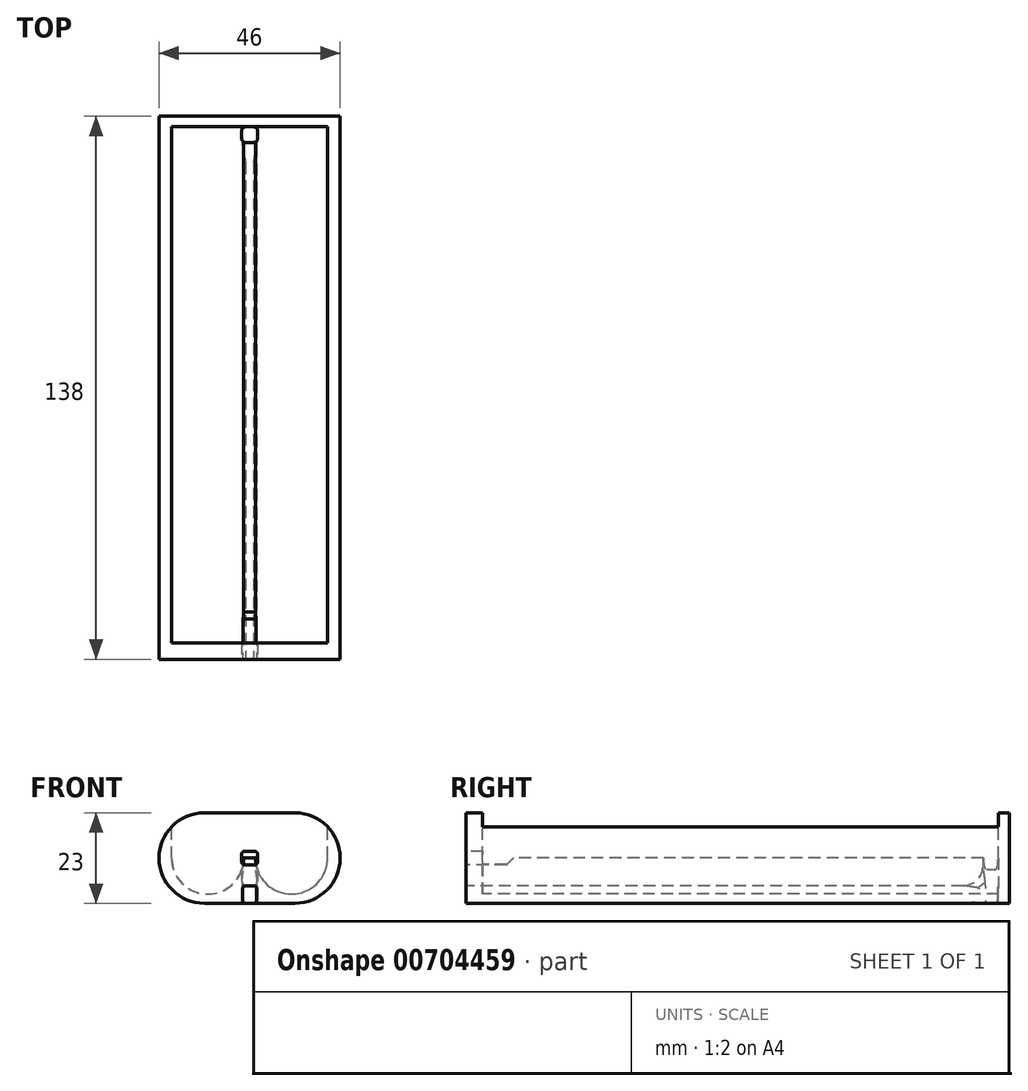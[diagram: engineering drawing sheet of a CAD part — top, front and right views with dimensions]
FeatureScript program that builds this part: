
annotation { "Feature Type Name" : "Feature", "Feature Type Description" : "" }
export const myFeature = defineFeature(function(context is Context, id is Id, definition is map)
    precondition{}
    {
        {
            var Q0;
            Q0=qCreatedBy(makeId("Front.planeOp"),FACE);
            var sketch = newSketch(context, id + "F0", { "sketchPlane" : qUnion([Q0])});
            skCircle(sketch, "E0", {"center": v(-11.5, 0) * mm, "radius": 11.5 * mm});
            skCircle(sketch, "E1", {"center": v(11.5, 0) * mm, "radius": 11.5 * mm});
            skLineSegment(sketch, "E2", {"start": v(-11.5, 11.5) * mm, "end": v(11.5, 11.5) * mm});
            skLineSegment(sketch, "E3", {"start": v(-11.5, -11.5) * mm, "end": v(11.5, -11.5) * mm});
            skSolve(sketch);
        }
        {
            var Q0;
            {var subQ0=sQuery(id+"F0.wireOp",EDGE,"E1");var subQ1=makeQuery(id+"F0.imprint","INTERSECT",VERTEX,{"derivedFrom":[subQ0,sQuery(id+"F0.wireOp",EDGE,"E2")]});Q0=makeQuery(id+"F0.imprint","IMPRINT",FACE,{"disambiguationData":[TD([[makeQuery(id+"F0.imprint","IMPRINT",EDGE,{"disambiguationData":[TD([[subQ1,1.0]])],"derivedFrom":subQ0}),1.0]])]});}
            var Q1;
            {var subQ0=sQuery(id+"F0.wireOp",EDGE,"E0");var subQ1=makeQuery(id+"F0.imprint","INTERSECT",VERTEX,{"derivedFrom":[subQ0,sQuery(id+"F0.wireOp",EDGE,"E3")]});Q1=makeQuery(id+"F0.imprint","IMPRINT",FACE,{"disambiguationData":[TD([[makeQuery(id+"F0.imprint","IMPRINT",EDGE,{"disambiguationData":[TD([[subQ1,-1.0]])],"derivedFrom":subQ0}),1.0]])]});}
            var Q2;
            {var subQ0=sQuery(id+"F0.wireOp",EDGE,"E2");Q2=makeQuery(id+"F0.imprint","IMPRINT",FACE,{"disambiguationData":[TD([[makeQuery(id+"F0.imprint","IMPRINT",EDGE,{"derivedFrom":subQ0}),-1.0]])]});}
            var Q3;
            {var subQ0=sQuery(id+"F0.wireOp",EDGE,"E3");Q3=makeQuery(id+"F0.imprint","IMPRINT",FACE,{"disambiguationData":[TD([[makeQuery(id+"F0.imprint","IMPRINT",EDGE,{"derivedFrom":subQ0}),1.0]])]});}
            extrude(context, id + "F1", {"entities" : qUnion([Q0, Q1, Q2, Q3]), "oppositeDirection" : true, "depth" : 138 * mm, "offsetDistance" : 25 * mm});
        }
        {
            var Q0;
            Q0=makeQuery(id+"F1.opExtrude","SWEPT_FACE",FACE,{"disambiguationData":[OSD([sQuery(id+"F0.wireOp",EDGE,"E2")])]});
            var sketch = newSketch(context, id + "F2", { "sketchPlane" : qUnion([Q0])});
            skLineSegment(sketch, "E4", {"start": v(0, 0) * mm, "end": v(0, 138) * mm, "construction": true});
            skLineSegment(sketch, "E5", {"start": v(0, 130.4) * mm, "end": v(18.2, 130.4) * mm, "construction": true});
            skLineSegment(sketch, "E6", {"start": v(0, 65.2) * mm, "end": v(18.2, 65.2) * mm, "construction": true});
            skLineSegment(sketch, "E7", {"start": v(0, 0) * mm, "end": v(18.2, 0) * mm, "construction": true});
            skSolve(sketch);
        }
        {
            var Q0;
            {var subQ0=sQuery(id+"F0.wireOp",EDGE,"E2");Q0=makeQuery(id+"F2.imprint","IMPRINT",FACE,{"disambiguationData":[TD([[makeQuery(id+"F2.imprint","IMPRINT",EDGE,{"derivedFrom":makeQuery(id+"F1.opExtrude","CAP_EDGE",EDGE,{"disambiguationData":[OSD([subQ0])],"isStart":true})}),1.0]])]});}
            var sketch = newSketch(context, id + "F3", { "sketchPlane" : qUnion([Q0])});
            skLineSegment(sketch, "E8.bottom", {"start": v(2.42, 69.2) * mm, "end": v(20.72, 69.2) * mm, "construction": true});
            skLineSegment(sketch, "E8.top", {"start": v(2.42, 4.2) * mm, "end": v(20.72, 4.2) * mm, "construction": true});
            skLineSegment(sketch, "E8.left", {"start": v(2.42, 69.2) * mm, "end": v(2.42, 4.2) * mm, "construction": true});
            skLineSegment(sketch, "E8.right", {"start": v(20.72, 69.2) * mm, "end": v(20.72, 4.2) * mm, "construction": true});
            skLineSegment(sketch, "E9.0.1.0", {"start": v(2.42, 135.3) * mm, "end": v(20.72, 135.3) * mm, "construction": true});
            skLineSegment(sketch, "E9.0.1.1", {"start": v(20.72, 135.3) * mm, "end": v(20.72, 70.3) * mm, "construction": true});
            skLineSegment(sketch, "E9.0.1.2", {"start": v(2.42, 135.3) * mm, "end": v(2.42, 70.3) * mm, "construction": true});
            skLineSegment(sketch, "E9.0.1.3", {"start": v(2.42, 70.3) * mm, "end": v(20.72, 70.3) * mm, "construction": true});
            skLineSegment(sketch, "E9.1.0.0", {"start": v(-20.68, 69.2) * mm, "end": v(-2.38, 69.2) * mm, "construction": true});
            skLineSegment(sketch, "E9.1.0.1", {"start": v(-2.38, 69.2) * mm, "end": v(-2.38, 4.2) * mm, "construction": true});
            skLineSegment(sketch, "E9.1.0.2", {"start": v(-20.68, 69.2) * mm, "end": v(-20.68, 4.2) * mm, "construction": true});
            skLineSegment(sketch, "E9.1.0.3", {"start": v(-20.68, 4.2) * mm, "end": v(-2.38, 4.2) * mm, "construction": true});
            skLineSegment(sketch, "E9.1.1.0", {"start": v(-20.68, 135.3) * mm, "end": v(-2.38, 135.3) * mm, "construction": true});
            skLineSegment(sketch, "E9.1.1.1", {"start": v(-2.38, 135.3) * mm, "end": v(-2.38, 70.3) * mm, "construction": true});
            skLineSegment(sketch, "E9.1.1.2", {"start": v(-20.68, 135.3) * mm, "end": v(-20.68, 70.3) * mm, "construction": true});
            skLineSegment(sketch, "E9.1.1.3", {"start": v(-20.68, 70.3) * mm, "end": v(-2.38, 70.3) * mm, "construction": true});
            skLineSegment(sketch, "E9.direction1", {"start": v(2.42, 4.2) * mm, "end": v(-20.68, 4.2) * mm, "construction": true});
            skLineSegment(sketch, "E9.direction2", {"start": v(2.42, 4.2) * mm, "end": v(2.42, 70.3) * mm, "construction": true});
            skSolve(sketch);
        }
        {
            var Q0;
            Q0=sQuery(id+"F3.wireOp",EDGE,"E8.top");
            var Q1;
            Q1=makeQuery(id+"F1.opExtrude","CAP_FACE",FACE,{"disambiguationData":[OSD([sQuery(id+"F0.wireOp",EDGE,"E0"),sQuery(id+"F0.wireOp",EDGE,"E1"),sQuery(id+"F0.wireOp",EDGE,"E2"),sQuery(id+"F0.wireOp",EDGE,"E3")])],"isStart":true});
            cPlane(context, id + "F4", {"entities" : qUnion([Q0, Q1]), "cplaneType" : CPlaneType.LINE_ANGLE, "offset" : 25 * mm, "angle" : 0 * degree, "width" : 150 * mm, "height" : 150 * mm});
        }
        {
            var Q0;
            Q0=qCreatedBy(id+"F4.planeOp",FACE);
            var sketch = newSketch(context, id + "F5", { "sketchPlane" : qUnion([Q0])});
            skCircle(sketch, "E10", {"center": v(-10.65, 0) * mm, "radius": 9.15 * mm});
            skCircle(sketch, "E11.MirrorC", {"center": v(10.65, 0) * mm, "radius": 9.15 * mm});
            skLineSegment(sketch, "E12", {"start": v(-19.8, 0) * mm, "end": v(-19.8, 11.5) * mm});
            skLineSegment(sketch, "E13", {"start": v(-19.8, 11.5) * mm, "end": v(19.8, 11.5) * mm});
            skLineSegment(sketch, "E14", {"start": v(19.8, 0) * mm, "end": v(19.8, 11.5) * mm});
            skLineSegment(sketch, "E15", {"start": v(1.5, 0) * mm, "end": v(-1.5, 0) * mm});
            skSolve(sketch);
        }
        {
            var Q0;
            Q0 = qSketchRegion(id + "F5", true);
            var Q1;
            Q1=sQuery(id+"F3.wireOp",VERTEX,"E9.0.1.0.start");
            extrude(context, id + "F6", {"entities" : qUnion([Q0]), "operationType" : NewBodyOperationType.REMOVE, "endBound" : BoundingType.UP_TO_VERTEX, "depth" : 25 * mm, "endBoundEntityVertex" : qUnion([Q1]), "offsetDistance" : 25 * mm});
        }
        {
            var Q0;
            Q0=makeQuery(id+"F1.opExtrude","CAP_FACE",FACE,{"disambiguationData":[OSD([sQuery(id+"F0.wireOp",EDGE,"E0"),sQuery(id+"F0.wireOp",EDGE,"E1"),sQuery(id+"F0.wireOp",EDGE,"E2"),sQuery(id+"F0.wireOp",EDGE,"E3")])],"isStart":true});
            var sketch = newSketch(context, id + "F7", { "sketchPlane" : qUnion([Q0])});
            skLineSegment(sketch, "E16.bottom", {"start": v(1, -11.5) * mm, "end": v(-1, -11.5) * mm});
            skLineSegment(sketch, "E16.top", {"start": v(1, -7) * mm, "end": v(-1, -7) * mm});
            skLineSegment(sketch, "E16.left", {"start": v(1.75, -10.75) * mm, "end": v(1.75, -7.75) * mm});
            skLineSegment(sketch, "E16.right", {"start": v(-1.75, -10.75) * mm, "end": v(-1.75, -7.75) * mm});
            skPoint(sketch, "E16.middle", {"position": v(0, -9.25) * mm});
            skPoint(sketch, "E17.visualSharp", {"position": v(1.75, -7) * mm});
            skArc(sketch, "E17.filletArc", {"start": v(1.75, -7.75) * mm, "mid": v(1.53, -7.22) * mm, "end": v(1, -7) * mm});
            skPoint(sketch, "E18.visualSharp", {"position": v(-1.75, -7) * mm});
            skArc(sketch, "E18.filletArc", {"start": v(-1, -7) * mm, "mid": v(-1.53, -7.22) * mm, "end": v(-1.75, -7.75) * mm});
            skPoint(sketch, "E19.visualSharp", {"position": v(-1.75, -11.5) * mm});
            skArc(sketch, "E19.filletArc", {"start": v(-1.75, -10.75) * mm, "mid": v(-1.53, -11.28) * mm, "end": v(-1, -11.5) * mm});
            skPoint(sketch, "E20.visualSharp", {"position": v(1.75, -11.5) * mm});
            skArc(sketch, "E20.filletArc", {"start": v(1, -11.5) * mm, "mid": v(1.53, -11.28) * mm, "end": v(1.75, -10.75) * mm});
            skSolve(sketch);
        }
        {
            var Q0;
            Q0=makeQuery(id+"F7.imprint","IMPRINT",FACE,{"disambiguationData":[TD([[makeQuery(id+"F7.imprint","IMPRINT",EDGE,{"derivedFrom":sQuery(id+"F7.wireOp",EDGE,"E16.bottom")}),1.0]])]});
            var Q1;
            Q1=makeQuery(id+"F6.boolean.opBoolean","COPY",FACE,{"derivedFrom":makeQuery(id+"F6.opExtrude","CAP_FACE",FACE,{"disambiguationData":[OSD([sQuery(id+"F5.wireOp",EDGE,"E10"),sQuery(id+"F5.wireOp",EDGE,"E11.MirrorC"),sQuery(id+"F5.wireOp",EDGE,"E12"),sQuery(id+"F5.wireOp",EDGE,"E13"),sQuery(id+"F5.wireOp",EDGE,"E14"),sQuery(id+"F5.wireOp",EDGE,"E15")])],"isStart":false})});
            extrude(context, id + "F8", {"entities" : qUnion([Q0]), "operationType" : NewBodyOperationType.REMOVE, "endBound" : BoundingType.UP_TO_SURFACE, "oppositeDirection" : true, "depth" : 25 * mm, "endBoundEntityFace" : qUnion([Q1]), "offsetDistance" : 25 * mm});
        }
        {
            var Q0;
            {var subQ0=sQuery(id+"F0.wireOp",EDGE,"E2");Q0=makeQuery(id+"F2.imprint","IMPRINT",FACE,{"disambiguationData":[TD([[makeQuery(id+"F2.imprint","IMPRINT",EDGE,{"derivedFrom":makeQuery(id+"F1.opExtrude","CAP_EDGE",EDGE,{"disambiguationData":[OSD([subQ0])],"isStart":true})}),1.0]])]});}
            var sketch = newSketch(context, id + "F9", { "sketchPlane" : qUnion([Q0])});
            skLineSegment(sketch, "E21.bottom", {"start": v(1, 135.3) * mm, "end": v(-1, 135.3) * mm});
            skLineSegment(sketch, "E21.top", {"start": v(1, 131.3) * mm, "end": v(-1, 131.3) * mm});
            skLineSegment(sketch, "E21.left", {"start": v(2, 134.3) * mm, "end": v(2, 132.3) * mm});
            skLineSegment(sketch, "E21.right", {"start": v(-2, 134.3) * mm, "end": v(-2, 132.3) * mm});
            skPoint(sketch, "E21.middle", {"position": v(0, 133.3) * mm});
            skPoint(sketch, "E22.visualSharp", {"position": v(2, 131.3) * mm});
            skArc(sketch, "E22.filletArc", {"start": v(1, 131.3) * mm, "mid": v(1.7, 131.6) * mm, "end": v(2, 132.3) * mm});
            skPoint(sketch, "E23.visualSharp", {"position": v(-2, 131.3) * mm});
            skArc(sketch, "E23.filletArc", {"start": v(-2, 132.3) * mm, "mid": v(-1.7, 131.6) * mm, "end": v(-1, 131.3) * mm});
            skPoint(sketch, "E24.visualSharp", {"position": v(-2, 135.3) * mm});
            skArc(sketch, "E24.filletArc", {"start": v(-1, 135.3) * mm, "mid": v(-1.7, 135) * mm, "end": v(-2, 134.3) * mm});
            skPoint(sketch, "E25.visualSharp", {"position": v(2, 135.3) * mm});
            skArc(sketch, "E25.filletArc", {"start": v(2, 134.3) * mm, "mid": v(1.7, 135) * mm, "end": v(1, 135.3) * mm});
            skSolve(sketch);
        }
        {
            var Q0;
            Q0 = qSketchRegion(id + "F9", true);
            extrude(context, id + "F10", {"entities" : qUnion([Q0]), "operationType" : NewBodyOperationType.REMOVE, "endBound" : BoundingType.THROUGH_ALL, "depth" : 25 * mm, "offsetDistance" : 25 * mm, "hasSecondDirection" : true, "secondDirectionBound" : BoundingType.THROUGH_ALL, "secondDirectionOppositeDirection" : true, "secondDirectionDepth" : 25 * mm});
        }
        {
            var Q0;
            Q0=makeQuery(id+"F10.boolean.opBoolean","INTERSECT",EDGE,{"derivedFrom":[makeQuery(id+"F8.boolean.opBoolean","COPY",FACE,{"derivedFrom":makeQuery(id+"F8.opExtrude","SWEPT_FACE",FACE,{"disambiguationData":[OSD([sQuery(id+"F7.wireOp",EDGE,"E16.top")])]})}),makeQuery(id+"F10.opExtrude","SWEPT_FACE",FACE,{"disambiguationData":[OSD([sQuery(id+"F9.wireOp",EDGE,"E21.top")])]})]});
            fillet(context, id + "F11", {"entities" : qUnion([Q0]), "tangentPropagation" : true, "radius" : 5 * mm, "defaultsChanged" : false, "vertexSettings" : [], "allowEdgeOverflow" : false});
        }
        {
            var Q0;
            Q0=makeQuery(id+"F1.opExtrude","CAP_FACE",FACE,{"disambiguationData":[OSD([sQuery(id+"F0.wireOp",EDGE,"E0"),sQuery(id+"F0.wireOp",EDGE,"E1"),sQuery(id+"F0.wireOp",EDGE,"E2"),sQuery(id+"F0.wireOp",EDGE,"E3")])],"isStart":true});
            var sketch = newSketch(context, id + "F12", { "sketchPlane" : qUnion([Q0])});
            skLineSegment(sketch, "E26.bottom", {"start": v(1.25, 1.75) * mm, "end": v(-1.25, 1.75) * mm});
            skLineSegment(sketch, "E26.top", {"start": v(1.25, -1.75) * mm, "end": v(-1.25, -1.75) * mm});
            skLineSegment(sketch, "E26.left", {"start": v(2, 1) * mm, "end": v(2, -1) * mm});
            skLineSegment(sketch, "E26.right", {"start": v(-2, 1) * mm, "end": v(-2, -1) * mm});
            skPoint(sketch, "E26.middle", {"position": v(0, 0) * mm});
            skPoint(sketch, "E27.visualSharp", {"position": v(2, 1.75) * mm});
            skArc(sketch, "E27.filletArc", {"start": v(2, 1) * mm, "mid": v(1.78, 1.53) * mm, "end": v(1.25, 1.75) * mm});
            skPoint(sketch, "E28.visualSharp", {"position": v(2, -1.75) * mm});
            skArc(sketch, "E28.filletArc", {"start": v(1.25, -1.75) * mm, "mid": v(1.78, -1.53) * mm, "end": v(2, -1) * mm});
            skPoint(sketch, "E29.visualSharp", {"position": v(-2, -1.75) * mm});
            skArc(sketch, "E29.filletArc", {"start": v(-2, -1) * mm, "mid": v(-1.78, -1.53) * mm, "end": v(-1.25, -1.75) * mm});
            skPoint(sketch, "E30.visualSharp", {"position": v(-2, 1.75) * mm});
            skArc(sketch, "E30.filletArc", {"start": v(-1.25, 1.75) * mm, "mid": v(-1.78, 1.53) * mm, "end": v(-2, 1) * mm});
            skSolve(sketch);
        }
        {
            var Q0;
            Q0 = qSketchRegion(id + "F12", true);
            extrude(context, id + "F13", {"entities" : qUnion([Q0]), "operationType" : NewBodyOperationType.REMOVE, "oppositeDirection" : true, "depth" : 10 * mm, "offsetDistance" : 25 * mm});
        }
        {
            var Q0;
            {var subQ1=sQuery(id+"F5.wireOp",EDGE,"E15");Q0=makeQuery(id+"F13.boolean.opBoolean","INTERSECT",EDGE,{"derivedFrom":[makeQuery(id+"F10.boolean.opBoolean","SPLIT",FACE,{"disambiguationData":[TD([makeQuery(id+"F10.opExtrude","SWEPT_FACE",FACE,{"disambiguationData":[OSD([sQuery(id+"F9.wireOp",EDGE,"E21.top")])]})])],"derivedFrom":makeQuery(id+"F6.boolean.opBoolean","COPY",FACE,{"derivedFrom":makeQuery(id+"F6.opExtrude","SWEPT_FACE",FACE,{"disambiguationData":[OSD([subQ1])]})})}),makeQuery(id+"F13.opExtrude","CAP_FACE",FACE,{"disambiguationData":[OSD([sQuery(id+"F12.wireOp",EDGE,"E26.bottom"),sQuery(id+"F12.wireOp",EDGE,"E26.top"),sQuery(id+"F12.wireOp",EDGE,"E26.left"),sQuery(id+"F12.wireOp",EDGE,"E26.right"),sQuery(id+"F12.wireOp",EDGE,"E27.filletArc"),sQuery(id+"F12.wireOp",EDGE,"E28.filletArc"),sQuery(id+"F12.wireOp",EDGE,"E29.filletArc"),sQuery(id+"F12.wireOp",EDGE,"E30.filletArc")])],"isStart":false})]});}
            chamfer(context, id + "F14", {"entities" : qUnion([Q0]), "width" : 2 * mm, "tangentPropagation" : true});
        }
    });
